# Revit family: Квайт_Екстра_Eng
name_source: partatom
category: Оборудование
units: mm (PartAtom-declared; Revit-internal decimal feet)

## family parameters
Всегда вертикально = Да
Классификация = Нет
На основе рабочей плоскости = Нет
Общий = Нет
При загрузке вырезать с полостями = Нет
Размер круглого соединителя = Использовать диаметр
Тип детали = Нормальный
Точка принадлежности помещению = Нет

## types (5) — shared parameters
00_20_Manufacturer = Vents
00_20_Name = Axial fan
Amperage = 0 А
Apparent Load = 23 Вт
B = 214 мм
Casing Material = Plastic, opaque, white
D = 148 мм
Diameter = 148 мм
Dy = 144 мм
Frequency = 50 Гц
Height = 214 мм
L = 111 мм
L1 = 32 мм
L2 = 79 мм
Length = 111 мм
Load Classification = HVAC
Maintenance zone material = <По категории>
Maximum Air Flow = 370.0 м³/ч
Number of Fase = 1
Power = 22 Вт
Sound pressure level at 3 m distance = 38 dBA
URL = https://ventilation-system.com
Voltage = 230 В
Weight = 1.33 кг
Width = 214 мм
Изготовитель = Vents
zero-valued in all types: Отметка по умолчанию

## per-type parameters (varying)
| type | 00_20_Type | Panel |
| 150 Quiet Extra Red | 150 Quiet Extra Red | Plastic red |
| 150 Quiet Extra Vintage | 150 Quiet Extra  Vintage | Plastic, opaque, white |
| 150 Quiet Extra Aluminum | 150 Quiet Extra Aluminum | Aluminum |
| 150 Quiet Extra Chrome | 150 Quiet Extra Chrome | Steeel Chrome |
| 150 Quiet Extra Black sapphire | 150 Quiet Extra Black sapphire | Plastic Black sapphire |
